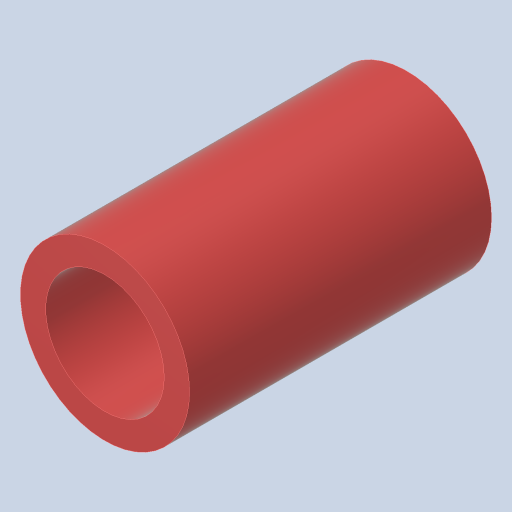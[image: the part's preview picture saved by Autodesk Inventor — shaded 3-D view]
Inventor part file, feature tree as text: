
AUTODESK INVENTOR PART (.ipt)
format: ipt  version: 2023.4 (Build 274418000, 418)  size: 123,392 bytes
history: native  units: in
note: dims shown in document units (in); Inventor stores cm internally (conversion verified against a paired STEP export)
features: extrude x1, sketch x1
ambient origin geometry x8: Origin, YZ Plane, XZ Plane, XY Plane, X Axis, Y Axis, Z Axis, Center Point
bodies: Solid1 (feature_tree)
feature tree (2):
  extrude  "Extrusion1"  Depth=1.49in
  sketch  "Sketch1"  dims[d0=0.585in d1=0.125in d2=1.49in d3=0.0in]
